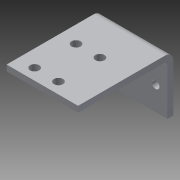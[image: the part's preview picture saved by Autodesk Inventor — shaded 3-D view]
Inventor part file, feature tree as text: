
AUTODESK INVENTOR PART (.ipt)
format: ipt  version: 2014 (Build 180170000, 170)  size: 128,512 bytes
history: native  units: in
note: dims shown in document units (in); Inventor stores cm internally (conversion verified against a paired STEP export)
features: sheet_metal_op x4, sketch x3, other x3
ambient origin geometry x8: Origin, YZ Plane, XZ Plane, XY Plane, X Axis, Y Axis, Z Axis, Center Point
bodies: Solid1 (feature_tree)
feature tree (10):
  sheet_metal_op  "Face1"
  sheet_metal_op  "Flange1"
  sketch  "Sketch1"  dims[d0=1.5in]
  other  "Plate1"
  sketch  "Sketch2"  dims[d1=1.0in]
  other  "Plate2"
  sheet_metal_op  "Bend1"
  sheet_metal_op  "Corner1"
  sketch  "Sketch3"  dims[d2=0.163in d3=0.5in d4=0.25in d5=0.7874in d7=1.0in d8=0.3937in d10=1.0in d12=0.125in d13=0.125in d14=0.0625in d15=0.25in d16=0.125in d17=2.0in d18=90.0deg d19=0.05in d20=0.5in d21=0.125in d22=0.125in d23=0.75in d24=1.31in d25=0.125in d26=0.22in d27=0.228in d28=0.5in d29=0.19in d30=0.125in d31=0.0in]
  other  "Cut1"
